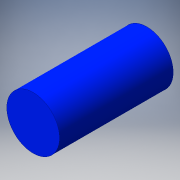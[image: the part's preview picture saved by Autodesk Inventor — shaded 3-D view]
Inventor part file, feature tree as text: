
AUTODESK INVENTOR PART (.ipt)
format: ipt  version: 2016 SP1 (Build 200210100, 210)  size: 94,208 bytes
history: native  units: in
note: dims shown in document units (in); Inventor stores cm internally (conversion verified against a paired STEP export)
features: other x3, sketch x1
ambient origin geometry x8: Origin, YZ Plane, XZ Plane, XY Plane, X Axis, Y Axis, Z Axis, Center Point
bodies: Solid1 (feature_tree)
feature tree (4):
  other  "Motor.ipt"
  other  "Solid1::Motor.ipt"
  other  "TaggingFeature1"
  sketch  "Sketch1"  dims[d0=0.3937in]
